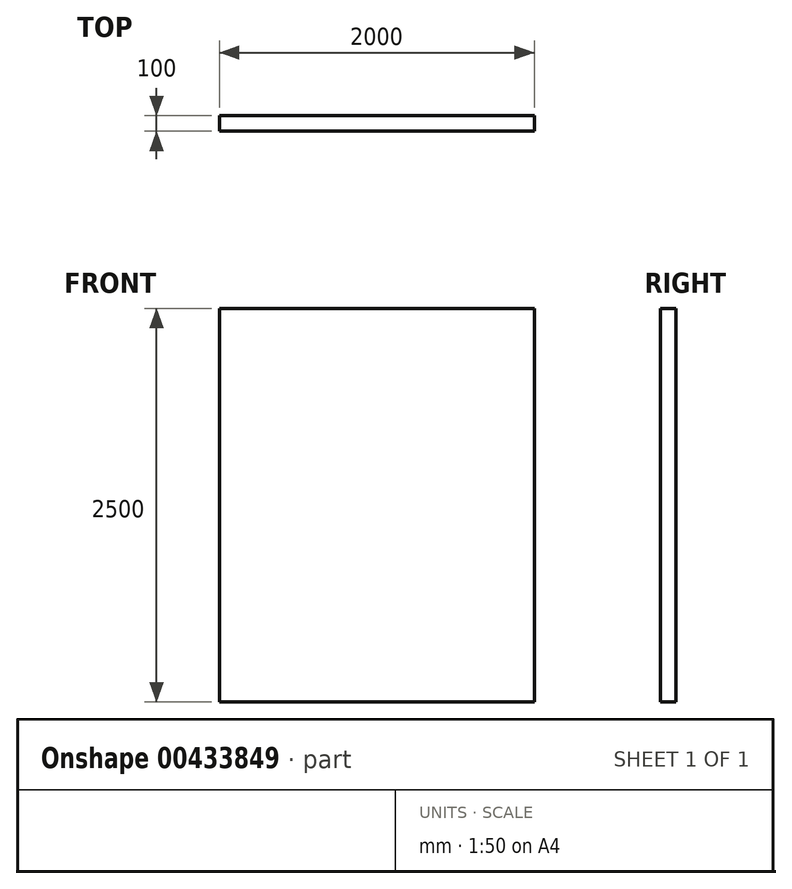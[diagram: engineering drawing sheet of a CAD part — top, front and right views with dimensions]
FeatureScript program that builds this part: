
annotation { "Feature Type Name" : "Feature", "Feature Type Description" : "" }
export const myFeature = defineFeature(function(context is Context, id is Id, definition is map)
    precondition{}
    {
        {
            var Q0;
            Q0=qCreatedBy(makeId("Top.planeOp"),FACE);
            var sketch = newSketch(context, id + "F0", { "sketchPlane" : qUnion([Q0])});
            skLineSegment(sketch, "E0", {"start": v(0, 0) * mm, "end": v(1000, 0) * mm});
            skLineSegment(sketch, "E1", {"start": v(1000, 0) * mm, "end": v(1000, 100) * mm});
            skLineSegment(sketch, "E2", {"start": v(1000, 100) * mm, "end": v(0, 100) * mm});
            skLineSegment(sketch, "E3.MirrorCS", {"start": v(-1000, 0) * mm, "end": v(-1000, 100) * mm});
            skLineSegment(sketch, "E4.MirrorCS", {"start": v(-1000, 100) * mm, "end": v(0, 100) * mm});
            skLineSegment(sketch, "E5.MirrorCS", {"start": v(0, 0) * mm, "end": v(-1000, 0) * mm});
            skSolve(sketch);
        }
        {
            var Q0;
            Q0=makeQuery(id+"F0.imprint","IMPRINT",FACE,{"disambiguationData":[TD([[makeQuery(id+"F0.imprint","IMPRINT",EDGE,{"derivedFrom":sQuery(id+"F0.wireOp",EDGE,"E0")}),1.0]])]});
            extrude(context, id + "F1", {"entities" : qUnion([Q0]), "depth" : 2500 * mm});
        }
    });
